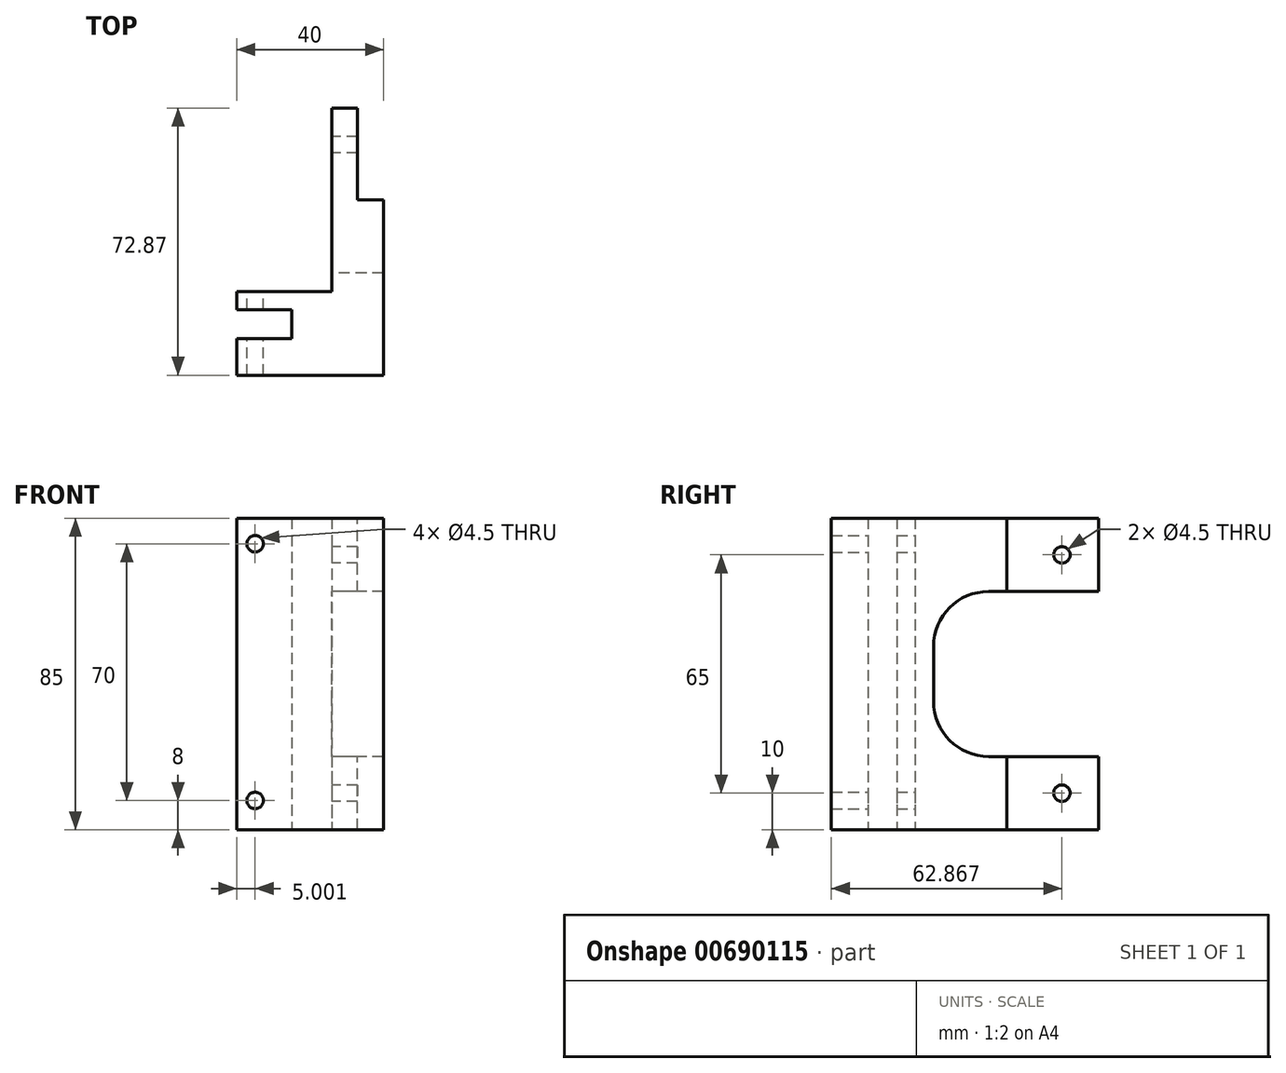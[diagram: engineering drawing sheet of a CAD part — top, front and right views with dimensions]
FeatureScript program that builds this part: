
annotation { "Feature Type Name" : "Feature", "Feature Type Description" : "" }
export const myFeature = defineFeature(function(context is Context, id is Id, definition is map)
    precondition{}
    {
        {
            var Q0;
            Q0=qCreatedBy(makeId("Top.planeOp"),FACE);
            var sketch = newSketch(context, id + "F0", { "sketchPlane" : qUnion([Q0])});
            skLineSegment(sketch, "E0.bottom", {"start": v(-30.37, 15.97) * mm, "end": v(-15.37, 15.97) * mm});
            skLineSegment(sketch, "E0.top", {"start": v(-30.37, -1.9) * mm, "end": v(9.63, -1.9) * mm});
            skLineSegment(sketch, "E0.left", {"start": v(-30.37, 8.1) * mm, "end": v(-30.37, -1.9) * mm});
            skLineSegment(sketch, "E1.top", {"start": v(-30.37, 8.1) * mm, "end": v(-15.37, 8.1) * mm});
            skLineSegment(sketch, "E1.right", {"start": v(-15.37, 15.97) * mm, "end": v(-15.37, 8.1) * mm});
            skLineSegment(sketch, "E2", {"start": v(-30.37, 15.97) * mm, "end": v(-30.37, 20.97) * mm});
            skLineSegment(sketch, "E3", {"start": v(-30.37, 20.97) * mm, "end": v(-4.48, 20.97) * mm});
            skLineSegment(sketch, "E4", {"start": v(9.63, 70.97) * mm, "end": v(9.63, -1.9) * mm});
            skLineSegment(sketch, "E5", {"start": v(-4.48, 20.97) * mm, "end": v(-4.48, 70.97) * mm});
            skLineSegment(sketch, "E6", {"start": v(-4.48, 70.97) * mm, "end": v(9.63, 70.97) * mm});
            skSolve(sketch);
        }
        {
            var Q0;
            Q0=makeQuery(id+"F0.imprint","IMPRINT",FACE,{"disambiguationData":[TD([[makeQuery(id+"F0.imprint","IMPRINT",EDGE,{"derivedFrom":sQuery(id+"F0.wireOp",EDGE,"E0.bottom")}),1.0]])]});
            extrude(context, id + "F1", {"entities" : qUnion([Q0]), "depth" : 85 * mm, "offsetDistance" : 25 * mm});
        }
        {
            var Q0;
            Q0=makeQuery(id+"F1.opExtrude","SWEPT_FACE",FACE,{"disambiguationData":[OSD([sQuery(id+"F0.wireOp",EDGE,"E3")])]});
            var sketch = newSketch(context, id + "F2", { "sketchPlane" : qUnion([Q0])});
            skCircle(sketch, "E7", {"center": v(25.37, 8) * mm, "radius": 2.25 * mm});
            skCircle(sketch, "E8", {"center": v(25.37, 78) * mm, "radius": 2.25 * mm});
            skSolve(sketch);
        }
        {
            var Q0;
            Q0=makeQuery(id+"F2.imprint","IMPRINT",FACE,{"disambiguationData":[TD([[makeQuery(id+"F2.imprint","IMPRINT",EDGE,{"derivedFrom":sQuery(id+"F2.wireOp",EDGE,"E7")}),1.0]])]});
            var Q1;
            Q1=makeQuery(id+"F2.imprint","IMPRINT",FACE,{"disambiguationData":[TD([[makeQuery(id+"F2.imprint","IMPRINT",EDGE,{"derivedFrom":sQuery(id+"F2.wireOp",EDGE,"E8")}),1.0]])]});
            extrude(context, id + "F3", {"entities" : qUnion([Q0, Q1]), "operationType" : NewBodyOperationType.REMOVE, "oppositeDirection" : true, "depth" : 50 * mm, "offsetDistance" : 25 * mm});
        }
        {
            var Q0;
            Q0=makeQuery(id+"F1.opExtrude","SWEPT_FACE",FACE,{"disambiguationData":[OSD([sQuery(id+"F0.wireOp",EDGE,"E5")])]});
            var sketch = newSketch(context, id + "F4", { "sketchPlane" : qUnion([Q0])});
            skCircle(sketch, "E9", {"center": v(-60.97, 10) * mm, "radius": 2.25 * mm});
            skCircle(sketch, "E10", {"center": v(-60.97, 75) * mm, "radius": 2.25 * mm});
            skLineSegment(sketch, "E11.bottom", {"start": v(-70.97, 20) * mm, "end": v(-40.97, 20) * mm});
            skLineSegment(sketch, "E11.top", {"start": v(-70.97, 65) * mm, "end": v(-40.97, 65) * mm});
            skLineSegment(sketch, "E11.left", {"start": v(-70.97, 20) * mm, "end": v(-70.97, 65) * mm});
            skLineSegment(sketch, "E11.right", {"start": v(-25.97, 35) * mm, "end": v(-25.97, 50) * mm});
            skPoint(sketch, "E12.visualSharp", {"position": v(-25.97, 65) * mm});
            skArc(sketch, "E12.filletArc", {"start": v(-25.97, 50) * mm, "mid": v(-30.36, 60.6) * mm, "end": v(-40.97, 65) * mm});
            skPoint(sketch, "E13.visualSharp", {"position": v(-25.97, 20) * mm});
            skArc(sketch, "E13.filletArc", {"start": v(-40.97, 20) * mm, "mid": v(-30.36, 24.4) * mm, "end": v(-25.97, 35) * mm});
            skSolve(sketch);
        }
        {
            var Q0;
            Q0=makeQuery(id+"F4.imprint","IMPRINT",FACE,{"disambiguationData":[TD([[makeQuery(id+"F4.imprint","IMPRINT",EDGE,{"derivedFrom":sQuery(id+"F4.wireOp",EDGE,"E11.bottom")}),1.0]])]});
            var Q1;
            Q1=makeQuery(id+"F4.imprint","IMPRINT",FACE,{"disambiguationData":[TD([[makeQuery(id+"F4.imprint","IMPRINT",EDGE,{"derivedFrom":sQuery(id+"F4.wireOp",EDGE,"E10")}),1.0]])]});
            var Q2;
            Q2=makeQuery(id+"F4.imprint","IMPRINT",FACE,{"disambiguationData":[TD([[makeQuery(id+"F4.imprint","IMPRINT",EDGE,{"derivedFrom":sQuery(id+"F4.wireOp",EDGE,"E9")}),1.0]])]});
            extrude(context, id + "F5", {"entities" : qUnion([Q0, Q1, Q2]), "operationType" : NewBodyOperationType.REMOVE, "oppositeDirection" : true, "depth" : 25 * mm, "offsetDistance" : 25 * mm});
        }
        {
            var Q0;
            Q0=makeQuery(id+"F1.opExtrude","CAP_FACE",FACE,{"disambiguationData":[OSD([sQuery(id+"F0.wireOp",EDGE,"E0.bottom"),sQuery(id+"F0.wireOp",EDGE,"E0.top"),sQuery(id+"F0.wireOp",EDGE,"E0.left"),sQuery(id+"F0.wireOp",EDGE,"E1.top"),sQuery(id+"F0.wireOp",EDGE,"E1.right"),sQuery(id+"F0.wireOp",EDGE,"E2"),sQuery(id+"F0.wireOp",EDGE,"E3"),sQuery(id+"F0.wireOp",EDGE,"E4"),sQuery(id+"F0.wireOp",EDGE,"E5"),sQuery(id+"F0.wireOp",EDGE,"E6")])],"isStart":false});
            var sketch = newSketch(context, id + "F6", { "sketchPlane" : qUnion([Q0])});
            skLineSegment(sketch, "E14", {"start": v(2.57, 70.97) * mm, "end": v(2.57, 45.97) * mm});
            skLineSegment(sketch, "E15", {"start": v(2.57, 45.97) * mm, "end": v(9.63, 45.97) * mm});
            skLineSegment(sketch, "E16", {"start": v(9.63, 45.97) * mm, "end": v(9.63, 70.97) * mm});
            skLineSegment(sketch, "E17", {"start": v(9.63, 70.97) * mm, "end": v(2.57, 70.97) * mm});
            skSolve(sketch);
        }
        {
            var Q0;
            Q0=makeQuery(id+"F6.imprint","IMPRINT",FACE,{"disambiguationData":[TD([[makeQuery(id+"F6.imprint","IMPRINT",EDGE,{"derivedFrom":sQuery(id+"F6.wireOp",EDGE,"E14")}),1.0]])]});
            extrude(context, id + "F7", {"entities" : qUnion([Q0]), "operationType" : NewBodyOperationType.REMOVE, "oppositeDirection" : true, "depth" : 85 * mm, "offsetDistance" : 25 * mm});
        }
    });
